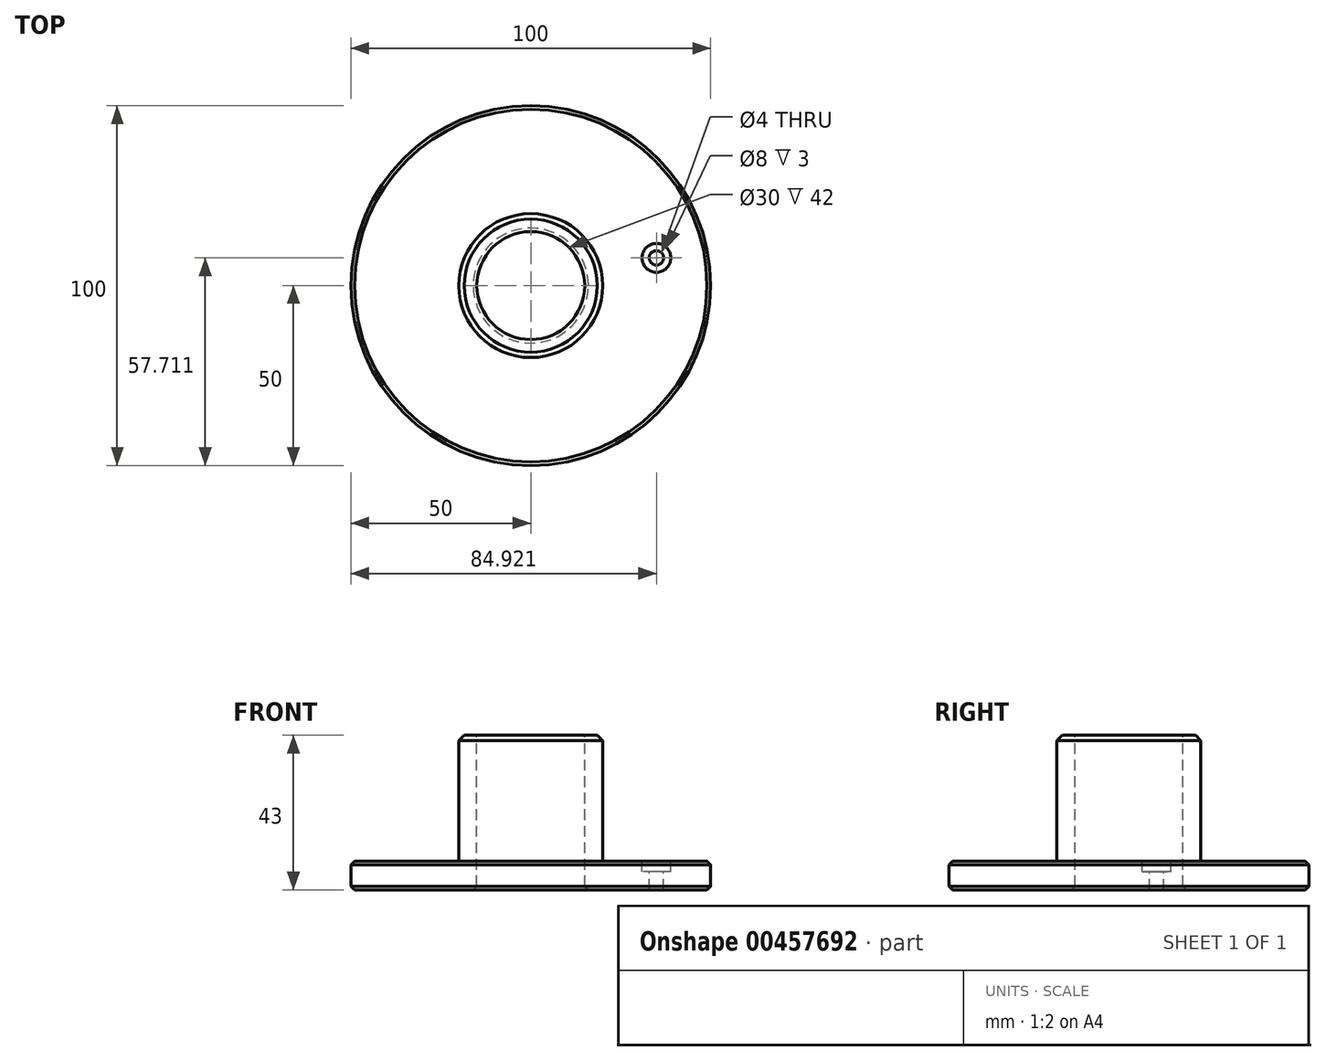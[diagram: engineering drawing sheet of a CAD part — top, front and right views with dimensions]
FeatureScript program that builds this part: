
annotation { "Feature Type Name" : "Feature", "Feature Type Description" : "" }
export const myFeature = defineFeature(function(context is Context, id is Id, definition is map)
    precondition{}
    {
        {
            var Q0;
            Q0=qCreatedBy(makeId("Top.planeOp"),FACE);
            var sketch = newSketch(context, id + "F0", { "sketchPlane" : qUnion([Q0])});
            skCircle(sketch, "E0", {"center": v(0, 0) * mm, "radius": 50 * mm});
            skSolve(sketch);
        }
        {
            var Q0;
            Q0=makeQuery(id+"F0.imprint","IMPRINT",FACE,{"disambiguationData":[TD([[makeQuery(id+"F0.imprint","IMPRINT",EDGE,{"derivedFrom":sQuery(id+"F0.wireOp",EDGE,"E0")}),1.0]])]});
            extrude(context, id + "F1", {"entities" : qUnion([Q0]), "depth" : 8 * mm});
        }
        {
            var Q0;
            Q0=makeQuery(id+"F1.opExtrude","CAP_FACE",FACE,{"disambiguationData":[OSD([sQuery(id+"F0.wireOp",EDGE,"E0")])],"isStart":false});
            var sketch = newSketch(context, id + "F2", { "sketchPlane" : qUnion([Q0])});
            skCircle(sketch, "E1", {"center": v(0, 0) * mm, "radius": 20 * mm});
            skSolve(sketch);
        }
        {
            var Q0;
            Q0=makeQuery(id+"F2.imprint","IMPRINT",FACE,{"disambiguationData":[TD([[makeQuery(id+"F2.imprint","IMPRINT",EDGE,{"derivedFrom":sQuery(id+"F2.wireOp",EDGE,"E1")}),1.0]])]});
            extrude(context, id + "F3", {"entities" : qUnion([Q0]), "operationType" : NewBodyOperationType.ADD, "depth" : 35 * mm});
        }
        {
            var Q0;
            Q0=makeQuery(id+"F1.opExtrude","CAP_FACE",FACE,{"disambiguationData":[OSD([sQuery(id+"F0.wireOp",EDGE,"E0")])],"isStart":false});
            var sketch = newSketch(context, id + "F4", { "sketchPlane" : qUnion([Q0])});
            skPoint(sketch, "E2", {"position": v(34.92, 7.71) * mm});
            skSolve(sketch);
        }
        {
            var Q0;
            Q0=sQuery(id+"F4.wireOp",VERTEX,"E2");
            var Q1;
            Q1=makeQuery(id+"F1.opExtrude","SWEPT_BODY",BODY,{"disambiguationData":[OSD([sQuery(id+"F0.wireOp",EDGE,"E0")])]});
            hole(context, id + "F5", {"style" : HoleStyle.C_BORE, "endStyle" : HoleEndStyle.BLIND, "holeDiameter" : 4 * mm, "cBoreDiameter" : 8 * mm, "cBoreDepth" : 3 * mm, "holeDepth" : 12 * mm, "isTappedThrough" : true, "tappedDepth" : 12 * mm, "tapClearance" : 3, "locations" : qUnion([Q0]), "scope" : qUnion([Q1])});
        }
        {
            var Q0;
            Q0=makeQuery(id+"F3.opExtrude","CAP_EDGE",EDGE,{"disambiguationData":[OSD([sQuery(id+"F2.wireOp",EDGE,"E1")])],"isStart":false});
            chamfer(context, id + "F6", {"entities" : qUnion([Q0]), "width" : 1.5 * mm, "tangentPropagation" : true});
        }
        {
            var Q0;
            Q0=makeQuery(id+"F3.opExtrude","CAP_FACE",FACE,{"disambiguationData":[OSD([sQuery(id+"F2.wireOp",EDGE,"E1")])],"isStart":false});
            var sketch = newSketch(context, id + "F7", { "sketchPlane" : qUnion([Q0])});
            skCircle(sketch, "E3.0", {"center": v(0, 0) * mm, "radius": 15 * mm});
            skSolve(sketch);
        }
        {
            var Q0;
            Q0=makeQuery(id+"F7.imprint","IMPRINT",FACE,{"disambiguationData":[TD([[makeQuery(id+"F7.imprint","IMPRINT",EDGE,{"derivedFrom":sQuery(id+"F7.wireOp",EDGE,"E3.0")}),1.0]])]});
            extrude(context, id + "F8", {"entities" : qUnion([Q0]), "operationType" : NewBodyOperationType.REMOVE, "endBound" : BoundingType.THROUGH_ALL, "oppositeDirection" : true, "depth" : 25 * mm});
        }
        {
            var Q0;
            Q0=makeQuery(id+"F1.opExtrude","CAP_EDGE",EDGE,{"disambiguationData":[OSD([sQuery(id+"F0.wireOp",EDGE,"E0")])],"isStart":false});
            var Q1;
            Q1=makeQuery(id+"F1.opExtrude","CAP_EDGE",EDGE,{"disambiguationData":[OSD([sQuery(id+"F0.wireOp",EDGE,"E0")])],"isStart":true});
            chamfer(context, id + "F9", {"entities" : qUnion([Q0, Q1]), "width" : 1 * mm, "tangentPropagation" : true});
        }
        {
            var Q0;
            Q0=makeQuery(id+"F8.boolean.opBoolean","INTERSECT",EDGE,{"derivedFrom":[makeQuery(id+"F1.opExtrude","CAP_FACE",FACE,{"disambiguationData":[OSD([sQuery(id+"F0.wireOp",EDGE,"E0")])],"isStart":true}),makeQuery(id+"F8.opExtrude","SWEPT_FACE",FACE,{"disambiguationData":[OSD([sQuery(id+"F7.wireOp",EDGE,"E3.0")])]})]});
            chamfer(context, id + "F10", {"entities" : qUnion([Q0]), "width" : 1 * mm, "tangentPropagation" : true});
        }
    });
